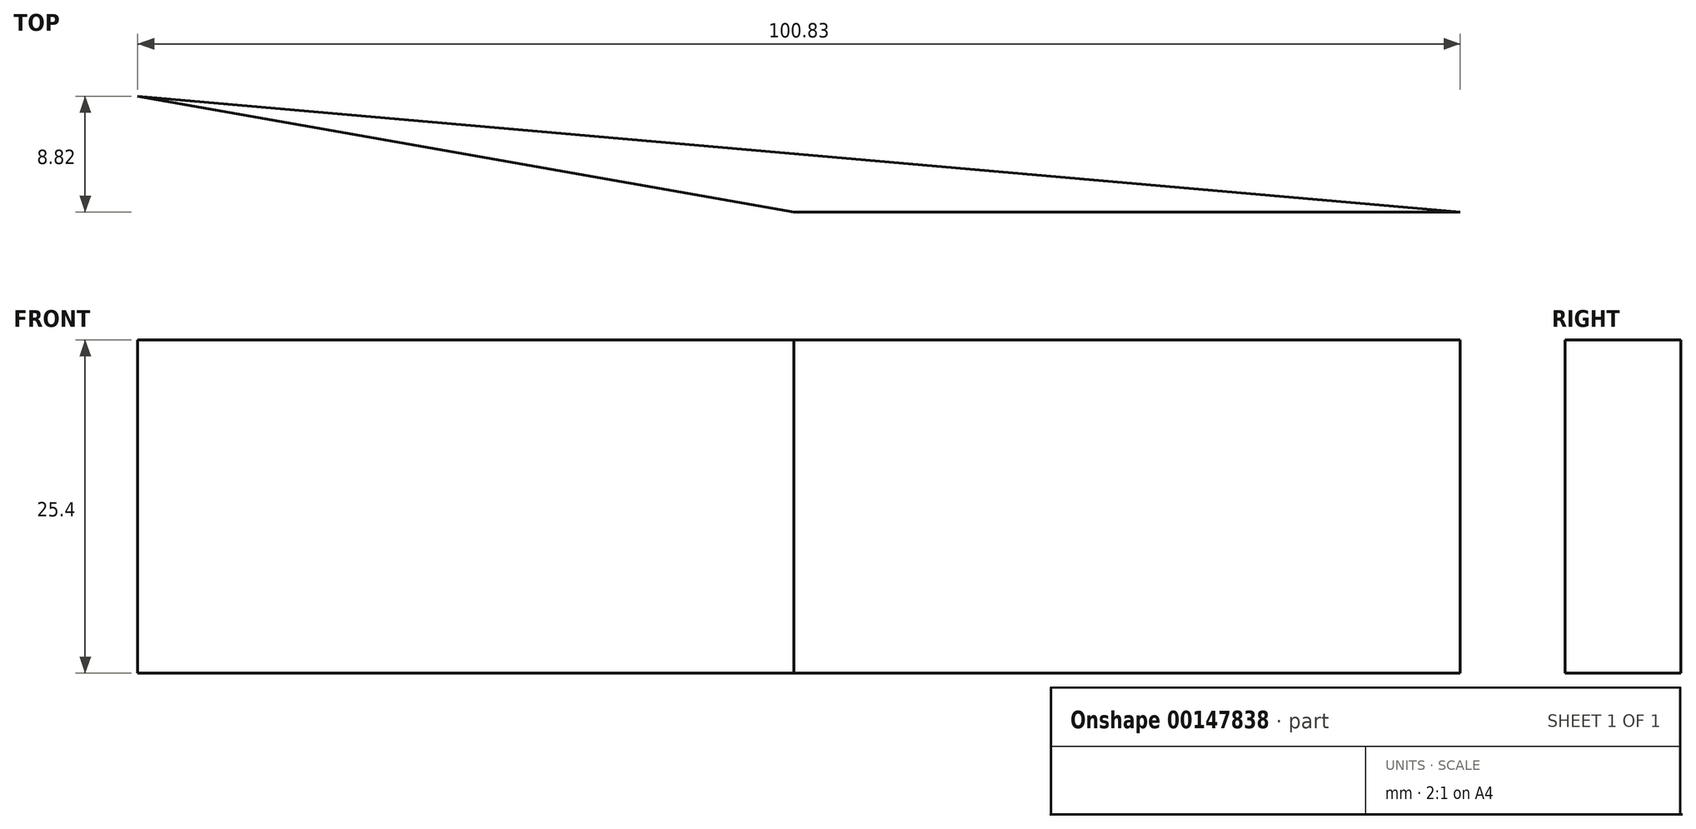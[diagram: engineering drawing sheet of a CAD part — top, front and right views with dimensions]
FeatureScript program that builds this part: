
annotation { "Feature Type Name" : "Feature", "Feature Type Description" : "" }
export const myFeature = defineFeature(function(context is Context, id is Id, definition is map)
    precondition{}
    {
        {
            var Q0;
            Q0=qCreatedBy(makeId("Top.planeOp"),FACE);
            var sketch = newSketch(context, id + "F0", { "sketchPlane" : qUnion([Q0])});
            skLineSegment(sketch, "E0.bottom", {"start": v(0, 0) * mm, "end": v(-50.8, 0) * mm});
            skLineSegment(sketch, "E1", {"start": v(-50.8, 0) * mm, "end": v(-100.83, 8.82) * mm});
            skLineSegment(sketch, "E2", {"start": v(0, 0) * mm, "end": v(-100.83, 8.82) * mm});
            skSolve(sketch);
        }
        {
            var Q0;
            Q0=makeQuery(id+"F0.imprint","IMPRINT",FACE,{"disambiguationData":[TD([[makeQuery(id+"F0.imprint","IMPRINT",EDGE,{"derivedFrom":sQuery(id+"F0.wireOp",EDGE,"E0.bottom")}),-1.0]])]});
            extrude(context, id + "F1", {"entities" : qUnion([Q0]), "depth" : 25.4 * mm});
        }
    });
